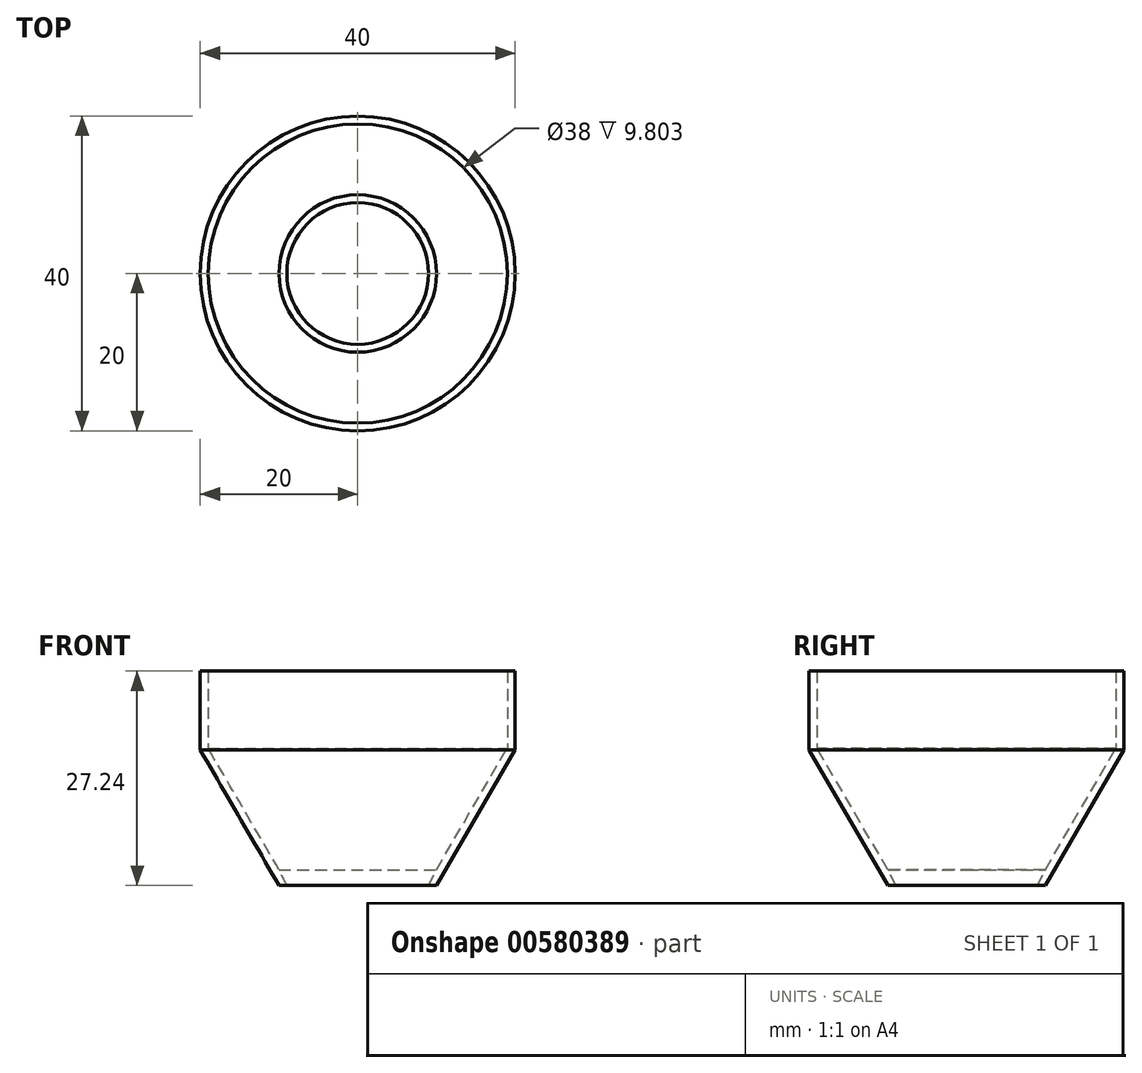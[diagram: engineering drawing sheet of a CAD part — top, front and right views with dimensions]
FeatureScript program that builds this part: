
annotation { "Feature Type Name" : "Feature", "Feature Type Description" : "" }
export const myFeature = defineFeature(function(context is Context, id is Id, definition is map)
    precondition{}
    {
        {
            var Q0;
            Q0=qCreatedBy(makeId("Front.planeOp"),FACE);
            var sketch = newSketch(context, id + "F0", { "sketchPlane" : qUnion([Q0])});
            skLineSegment(sketch, "E0", {"start": v(0, 0) * mm, "end": v(-10, 0) * mm});
            skLineSegment(sketch, "E1", {"start": v(-15.52, 27.24) * mm, "end": v(-15.52, 27.28) * mm});
            skLineSegment(sketch, "E2", {"start": v(0, 0) * mm, "end": v(0, 16.58) * mm});
            skPoint(sketch, "E3.start.orphan", {"position": v(-12.72, 23.31) * mm});
            skLineSegment(sketch, "E4", {"start": v(-12.72, 27.24) * mm, "end": v(-12.72, 27.28) * mm});
            skPoint(sketch, "E5.end.orphan", {"position": v(0, 23.02) * mm});
            skLineSegment(sketch, "E6", {"start": v(-19, 27.24) * mm, "end": v(-20, 27.24) * mm});
            skLineSegment(sketch, "E7", {"start": v(-20, 27.24) * mm, "end": v(-20, 17.24) * mm});
            skLineSegment(sketch, "E8", {"start": v(-10, 0) * mm, "end": v(-20, 17.24) * mm});
            skLineSegment(sketch, "E9", {"start": v(-10, 0) * mm, "end": v(-10, 2) * mm});
            skLineSegment(sketch, "E10", {"start": v(-19, 27.24) * mm, "end": v(-19, 17.43) * mm});
            skLineSegment(sketch, "E11", {"start": v(-20, 27.24) * mm, "end": v(-19, 27.24) * mm});
            skLineSegment(sketch, "E12", {"start": v(-10, 2) * mm, "end": v(-10.82, 3.41) * mm});
            skLineSegment(sketch, "E13", {"start": v(-11.69, 2.9) * mm, "end": v(-10.82, 3.41) * mm});
            skLineSegment(sketch, "E14", {"start": v(-10.82, 3.41) * mm, "end": v(-19, 17.43) * mm});
            skLineSegment(sketch, "E15", {"start": v(-10, 0) * mm, "end": v(-10, -5) * mm});
            skLineSegment(sketch, "E16", {"start": v(-10, -5) * mm, "end": v(-9, -5) * mm});
            skLineSegment(sketch, "E17", {"start": v(-10, 2) * mm, "end": v(-9, 0) * mm});
            skSolve(sketch);
        }
        {
            var Q0;
            Q0 = qSketchRegion(id + "F0", true);
            var Q1;
            Q1=sQuery(id+"F0.wireOp",EDGE,"E2");
            revolve(context, id + "F1", {"entities" : qUnion([Q0]), "axis" : qUnion([Q1]), "revolveType" : RevolveType.FULL});
        }
    });
